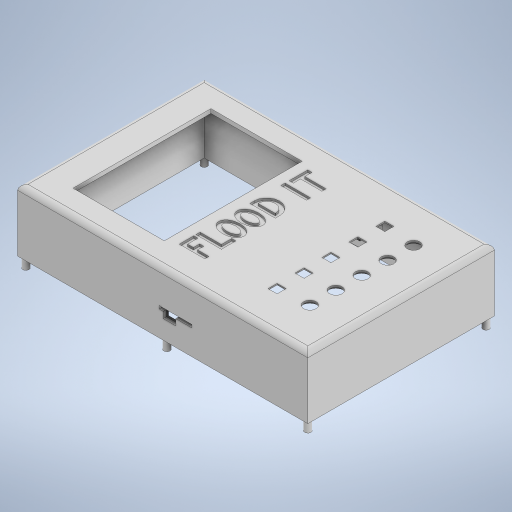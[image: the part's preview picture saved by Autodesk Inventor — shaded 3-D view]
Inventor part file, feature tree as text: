
AUTODESK INVENTOR PART (.ipt)
format: ipt  version: 2023 (Build 270158000, 158)  size: 709,632 bytes
history: native  units: in
note: dims shown in document units (in); Inventor stores cm internally (conversion verified against a paired STEP export)
features: extrude x16, sketch x14, fillet x2
ambient origin geometry x8: Origin, YZ Plane, XZ Plane, XY Plane, X Axis, Y Axis, Z Axis, Center Point
bodies: Solid1 (feature_tree)
feature tree (32):
  extrude  "Extrusion1"  Depth=4.5in
  extrude  "Extrusion2"  Depth=0.2in
  fillet  "Fillet1"  Radius=1.4in
  extrude  "Extrusion3"  Depth=0.125in
  extrude  "Extrusion4"  Depth=2.2in
  extrude  "Extrusion5"  Depth=0.5875in
  sketch  "Sketch6"  dims[d13=0.75in d14=1.4in d15=0.0in]
  extrude  "Extrusion6"  Depth=1.4in TaperAngle=0.0deg
  extrude  "Extrusion9"  Depth=0.1in
  extrude  "Extrusion10"  Depth=0.1in
  extrude  "Extrusion11"  Depth=0.25in
  extrude  "Extrusion12"  Depth=0.15in
  extrude  "Extrusion13"  Depth=0.7in
  extrude  "Extrusion14"  Depth=0.1in
  extrude  "Extrusion15"  Depth=0.615in
  extrude  "Extrusion16"  Depth=0.0625in
  fillet  "Fillet2"  Radius=0.21in
  extrude  "Extrusion18"  Depth=0.0625in
  extrude  "Extrusion19"  Depth=0.0625in
  sketch  "Sketch1"  dims[d0=7.0in d1=4.5in]
  sketch  "Sketch2"  dims[d2=1.5in d3=0.0in d4=0.2in d5=1.4in d6=0.0in]
  sketch  "Sketch3"  dims[d7=0.125in d8=0.25in]
  sketch  "Sketch4"  dims[d9=0.25in d10=2.2in]
  sketch  "Sketch5"  dims[d11=3.325in d12=0.5875in]
  sketch  "Sketch8"  dims[d16=0.1in d17=0.14in]
  sketch  "Sketch9"  dims[d18=0.1in d19=0.275in]
  sketch  "Sketch10"  dims[d20=0.35in d21=0.25in]
  sketch  "Sketch11"  dims[d22=0.15in d23=0.15in]
  sketch  "Sketch12"  dims[d24=0.25in d25=0.7in]
  sketch  "Sketch13"  dims[d26=0.1in d27=0.1in]
  sketch  "Sketch15"  dims[d28=0.25in d29=0.615in]
  sketch  "Sketch16"  dims[d30=0.25in d31=1.1in d32=0.21in d33=0.3075in d34=0.5575in d35=1.65in d36=0.3075in d37=0.21in d38=0.5575in d39=2.1in d40=0.1in d41=0.1in d42=0.3in d43=0.1in d44=0.25in d45=0.615in d46=2.4in d47=0.11in d48=2.51in d49=0.5575in d50=0.1in d51=0.615in d52=0.175in d53=0.175in d54=0.1in d55=0.1in d56=0.25in d57=3.15in d58=0.1in d59=0.515in d60=0.05in d61=0.0in d62=0.1125in d63=0.1125in d64=0.2175in d65=0.2175in d66=0.2175in d67=0.2175in d68=0.2175in d69=0.2175in d70=0.65in d71=0.65in d72=0.65in d73=0.65in d74=0.8413in d76=2.25in d77=0.3in d78=0.3in d79=0.3in d80=0.3in d81=0.3in d82=0.625in d83=0.625in d84=0.625in d85=0.625in d86=1.0in d87=3.1in d88=3.1in d89=3.1in d90=3.1in d91=3.1in d92=1.0in d93=0.0in d97=0.4in d98=0.4in d99=0.4in d100=0.4in d101=0.4in d102=0.05in d103=0.0in d124=0.0688in d125=0.0in d126=0.25in d127=0.275in d128=0.25in d129=0.25in d130=0.25in d131=2.1in d132=0.2in d134=0.05in d135=0.0in d142=0.0375in d143=0.0in d144=2.0in d145=0.785in d146=0.0725in d147=0.3in d148=0.15in d149=0.1in d150=0.7in d151=0.2in d152=0.0in d153=0.075in d154=0.125in d155=0.0in d156=0.285in d157=2.5in d158=0.49in d159=0.25in d160=0.0in d161=0.49in d162=0.081in d163=0.0in d164=0.45in d177=0.075in d178=0.0in d179=0.125in d187=2.8in d189=0.04in d190=0.04in d191=0.04in d192=0.04in d193=0.04in d194=0.485in d195=0.0938in d197=3.325in d198=0.254in d199=0.1735in d202=0.075in d203=0.125in d204=0.075in d205=0.125in d206=0.1875in d207=0.1875in d208=0.1875in d209=0.65in d210=0.65in d211=0.65in d212=0.125in d213=0.075in d214=0.025in d215=2.0in d216=0.5in d217=0.0in d218=0.0in d219=0.285in d220=0.1425in d221=0.245in d222=0.285in d224=0.8413in d225=0.15in d226=0.15in d227=0.15in d228=0.15in d229=0.15in d230=0.15in d231=0.1in d232=0.1in d233=0.1in d234=0.1in d235=0.1in d236=0.1in d237=0.1in d238=0.1in d239=0.1in d240=0.1in d241=3.5in d242=3.5in d243=0.245in d244=0.0in d245=0.0625in]
